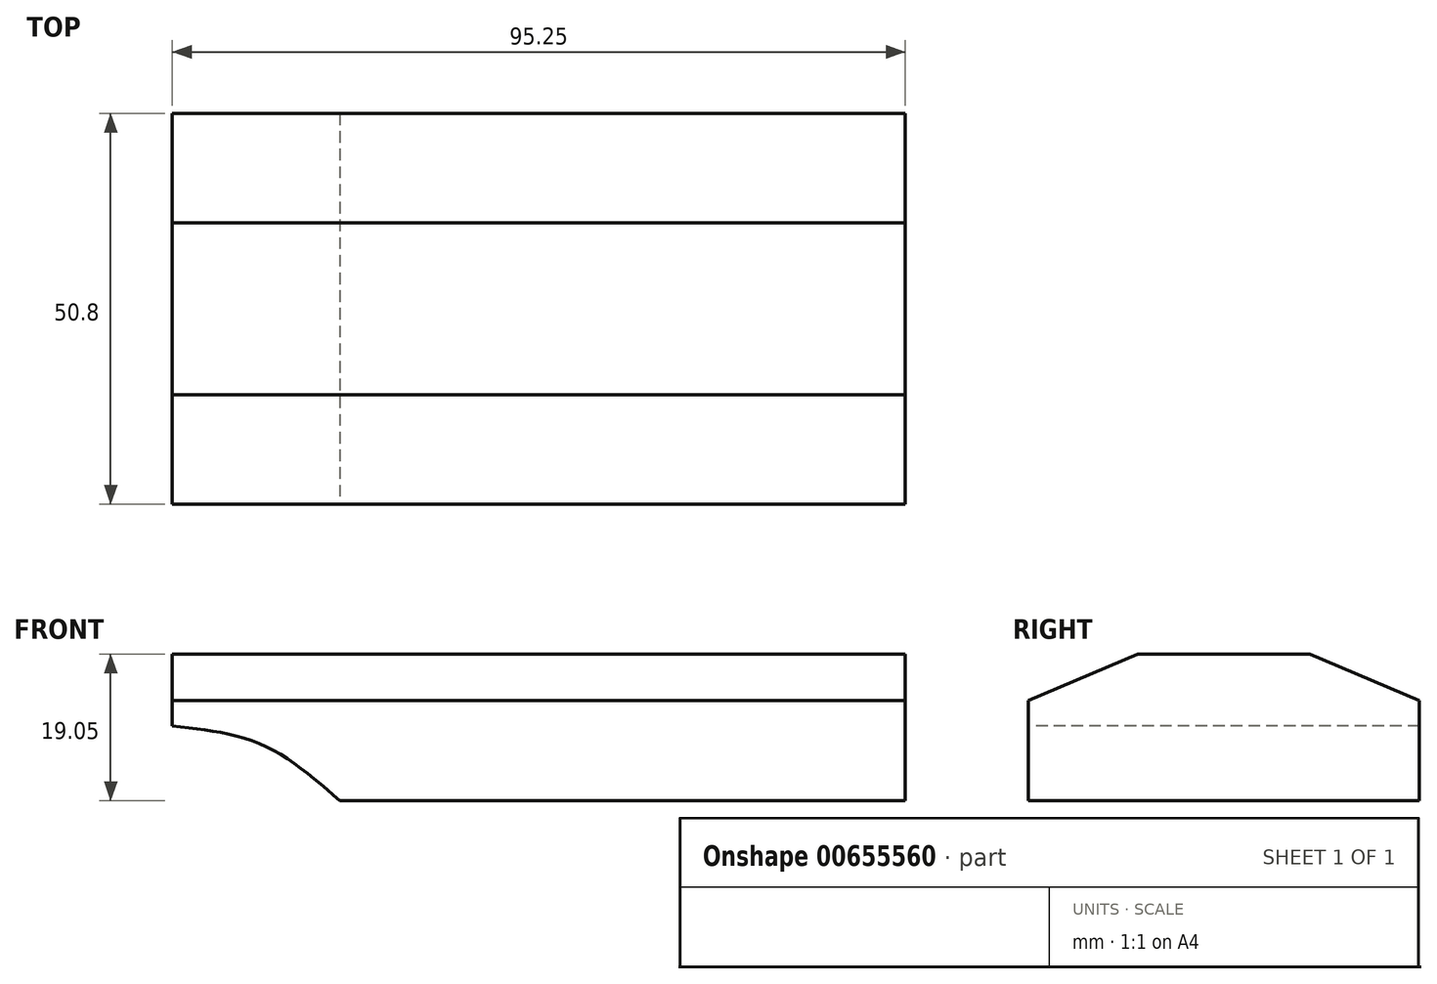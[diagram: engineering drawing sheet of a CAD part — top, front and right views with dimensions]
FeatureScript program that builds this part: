
annotation { "Feature Type Name" : "Feature", "Feature Type Description" : "" }
export const myFeature = defineFeature(function(context is Context, id is Id, definition is map)
    precondition{}
    {
        {
            var Q0;
            Q0=qCreatedBy(makeId("Right.planeOp"),FACE);
            var sketch = newSketch(context, id + "F0", { "sketchPlane" : qUnion([Q0])});
            skLineSegment(sketch, "E0", {"start": v(0, 20.19) * mm, "end": v(0, -17.1) * mm, "construction": true});
            skLineSegment(sketch, "E1", {"start": v(0, 9.36) * mm, "end": v(11.16, 9.36) * mm});
            skLineSegment(sketch, "E2", {"start": v(11.16, 9.36) * mm, "end": v(25.4, 3.34) * mm});
            skLineSegment(sketch, "E3", {"start": v(25.4, 3.34) * mm, "end": v(25.4, -9.69) * mm});
            skLineSegment(sketch, "E4", {"start": v(25.4, -9.69) * mm, "end": v(0, -9.69) * mm});
            skLineSegment(sketch, "E5.MirrorCS", {"start": v(0, 9.36) * mm, "end": v(-11.16, 9.36) * mm});
            skLineSegment(sketch, "E6.MirrorCS", {"start": v(-11.16, 9.36) * mm, "end": v(-25.4, 3.34) * mm});
            skLineSegment(sketch, "E7.MirrorCS", {"start": v(-25.4, 3.34) * mm, "end": v(-25.4, -9.69) * mm});
            skLineSegment(sketch, "E8.MirrorCS", {"start": v(-25.4, -9.69) * mm, "end": v(0, -9.69) * mm});
            skSolve(sketch);
        }
        {
            var Q0;
            Q0 = qSketchRegion(id + "F0", true);
            extrude(context, id + "F1", {"entities" : qUnion([Q0]), "depth" : 95.25 * mm, "offsetDistance" : 25.4 * mm});
        }
        {
            var Q0;
            Q0=makeQuery(id+"F1.opExtrude","SWEPT_FACE",FACE,{"disambiguationData":[OSD([sQuery(id+"F0.wireOp",EDGE,"E7.MirrorCS")])]});
            var sketch = newSketch(context, id + "F2", { "sketchPlane" : qUnion([Q0])});
            skFitSpline(sketch, "E9", {"points": [v(0, 0) * mm, v(11.6, -2.39) * mm, v(21.79, -9.69) * mm], "startDerivative": vector(24.39, -2.5) * mm, "endDerivative": vector(19.21, -16.82) * mm});
            skLineSegment(sketch, "E10", {"start": v(0, 0) * mm, "end": v(0, -9.69) * mm});
            skLineSegment(sketch, "E11", {"start": v(0, -9.69) * mm, "end": v(21.79, -9.69) * mm});
            skSolve(sketch);
        }
        {
            var Q0;
            Q0=makeQuery(id+"F2.imprint","IMPRINT",FACE,{"disambiguationData":[TD([[makeQuery(id+"F2.imprint","IMPRINT",EDGE,{"derivedFrom":sQuery(id+"F2.wireOp",EDGE,"E9")}),-1.0]])]});
            extrude(context, id + "F3", {"entities" : qUnion([Q0]), "operationType" : NewBodyOperationType.REMOVE, "oppositeDirection" : true, "depth" : 50.8 * mm, "offsetDistance" : 25.4 * mm});
        }
    });
